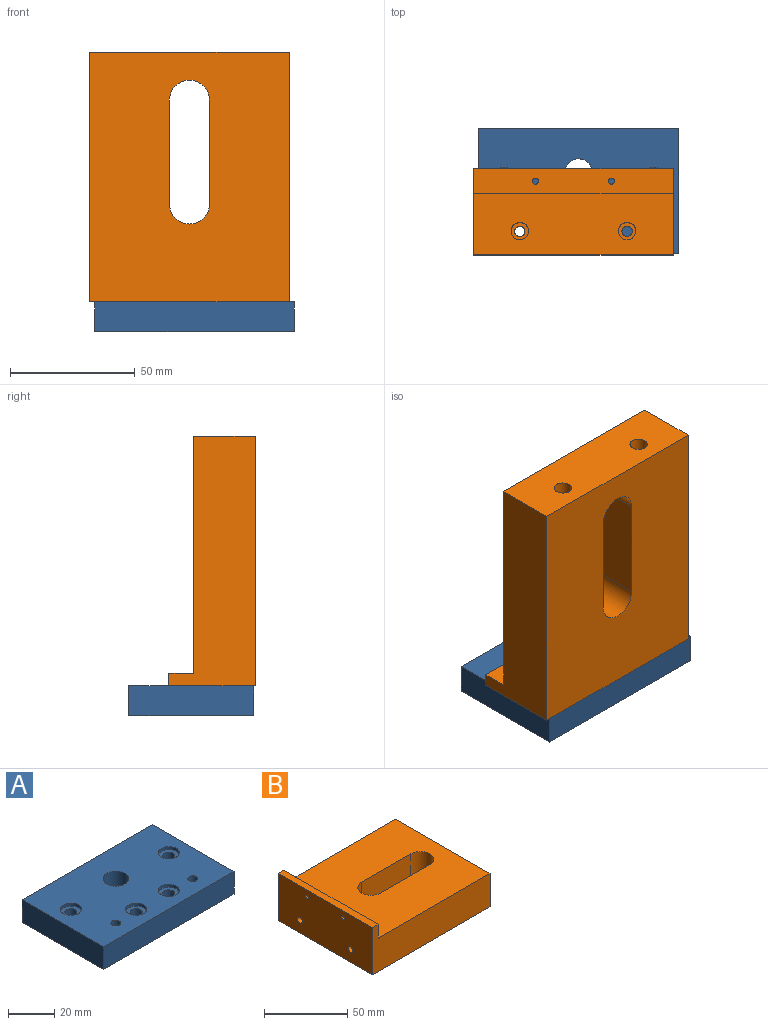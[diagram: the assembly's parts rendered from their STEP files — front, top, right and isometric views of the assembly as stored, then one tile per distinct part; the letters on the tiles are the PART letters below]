
ASSEMBLY  parts=2 mates=1
PART A: 27 faces, bbox 80x50x12 mm
  f0: cylinder r=8.05mm len=16.1mm, axis (0,0,-1), area 227.6mm2, adj f17,f26
  f1: cylinder r=2.1mm len=14mm, axis (0,1,0), area 184.7mm2, adj f2,f21
  f2: cone r=2.1mm half-angle=59deg, axis (0,1,0), area 16.2mm2, adj f1
  f3: cylinder r=2.1mm len=14mm, axis (0,1,0), area 184.7mm2, adj f4,f21
  f4: cone r=2.1mm half-angle=59deg, axis (0,1,0), area 16.2mm2, adj f3
  f5: cylinder r=2.1mm len=12mm, axis (0,0,1), area 158.3mm2, adj f16,f17
  f6: cylinder r=2.1mm len=12mm, axis (0,0,1), area 158.3mm2, adj f16,f17
  f7: cylinder r=4.6mm len=9.2mm, axis (0,0,1), area 44.8mm2, adj f16,f25
  f8: cylinder r=4.6mm len=9.2mm, axis (0,0,1), area 44.8mm2, adj f16,f24
  f9: cylinder r=4.6mm len=9.2mm, axis (0,0,1), area 44.8mm2, adj f16,f23
  f10: cylinder r=4.6mm len=9.2mm, axis (0,0,1), area 44.8mm2, adj f16,f22
  f11: cylinder r=2.6mm len=10.45mm, axis (0,0,-1), area 170.7mm2, adj f17,f22
  f12: cylinder r=2.6mm len=10.45mm, axis (0,0,-1), area 170.7mm2, adj f17,f23
  f13: cylinder r=2.6mm len=10.45mm, axis (0,0,-1), area 170.7mm2, adj f17,f24
  f14: cylinder r=2.6mm len=10.45mm, axis (0,0,-1), area 170.7mm2, adj f17,f25
  f15: cylinder r=5.59mm len=11.18mm, axis (0,0,-1), area 263.3mm2, adj f16,f26
  f16: plane 80x50mm, normal (0,0,1), area 3608.3mm2, adj f5,f6,f7,f8,f9,f10,f15,f18
  f17: plane 80x50mm, normal (0,0,-1), area 3683.8mm2, adj f0,f5,f6,f11,f12,f13,f14,f18
  f18: plane 50x12mm, normal (-1,0,0), area 600mm2, adj f16,f17,f19,f21
  f19: plane 80x12mm, normal (0,-1,0), area 960mm2, adj f16,f17,f18,f20
  f20: plane 50x12mm, normal (1,0,0), area 600mm2, adj f16,f17,f19,f21
  f21: plane 80x12mm, normal (0,1,0), area 932.3mm2, adj f1,f3,f16,f17,f18,f20
  f22: plane 9.2x9.2mm, normal (0,0,1), area 45.2mm2, adj f10,f11
  f23: plane 9.2x9.2mm, normal (0,0,1), area 45.2mm2, adj f9,f12
  f24: plane 9.2x9.2mm, normal (0,0,1), area 45.2mm2, adj f8,f13
  f25: plane 9.2x9.2mm, normal (0,0,1), area 45.2mm2, adj f7,f14
  f26: plane 16.1x16.1mm, normal (0,0,-1), area 105.5mm2, adj f0,f15
PART B: 20 faces, bbox 100x80x34.6 mm
  f0: cylinder r=1.23mm len=5mm, axis (1,0,0), area 38.6mm2, adj f2,f19
  f1: cylinder r=1.23mm len=5mm, axis (1,0,0), area 38.6mm2, adj f2,f19
  f2: plane 80x10mm, normal (1,0,0), area 790.5mm2, adj f0,f1,f3,f14,f16,f17
  f3: plane 80x5mm, normal (0,0,1), area 400mm2, adj f2,f14,f16,f19
  f4: cylinder r=8mm len=24.6mm, axis (0,0,-1), area 618.3mm2, adj f5,f7,f15,f17
  f5: plane 41.7x24.6mm, normal (0,-1,0), area 1025.7mm2, adj f4,f6,f15,f17
  f6: cylinder r=8mm len=24.6mm, axis (0,0,-1), area 618.3mm2, adj f5,f7,f15,f17
  f7: plane 41.7x24.6mm, normal (0,1,0), area 1025.7mm2, adj f4,f6,f15,f17
  f8: plane 7x7mm, normal (1,0,0), area 25.1mm2, adj f9,f10
  f9: cylinder r=3.5mm len=90mm, axis (1,0,0), area 1979.2mm2, adj f8,f18
  f10: cylinder r=2.07mm len=10mm, axis (1,0,0), area 129.9mm2, adj f8,f19
  f11: plane 7x7mm, normal (1,0,0), area 25.1mm2, adj f12,f13
  f12: cylinder r=3.5mm len=90mm, axis (1,0,0), area 1979.2mm2, adj f11,f18
  f13: cylinder r=2.07mm len=10mm, axis (1,0,0), area 129.9mm2, adj f11,f19
  f14: plane 100x34.6mm, normal (0,1,0), area 2510mm2, adj f2,f3,f15,f17,f18,f19
  f15: plane 100x80mm, normal (0,0,-1), area 7131.8mm2, adj f4,f5,f6,f7,f14,f16,f18,f19
  f16: plane 100x34.6mm, normal (0,-1,0), area 2510mm2, adj f2,f3,f15,f17,f18,f19
  f17: plane 95x80mm, normal (0,0,1), area 6731.8mm2, adj f2,f4,f5,f6,f7,f14,f16,f18
  f18: plane 80x24.6mm, normal (1,0,0), area 1891mm2, adj f9,f12,f14,f15,f16,f17
  f19: plane 80x34.6mm, normal (-1,0,0), area 2731.7mm2, adj f0,f1,f3,f10,f13,f14,f15,f16
PLACE A t=(-2.21,-37.74,-57.84)mm
PLACE B rot(axis=(-0.58,-0.58,-0.58),120deg) t=(27.07,-25.39,-45.84)mm
MATE fastened B.f12 <-> A.f5  axis (0,0,-1) through (14.22,-28.84,-45.84)mm
